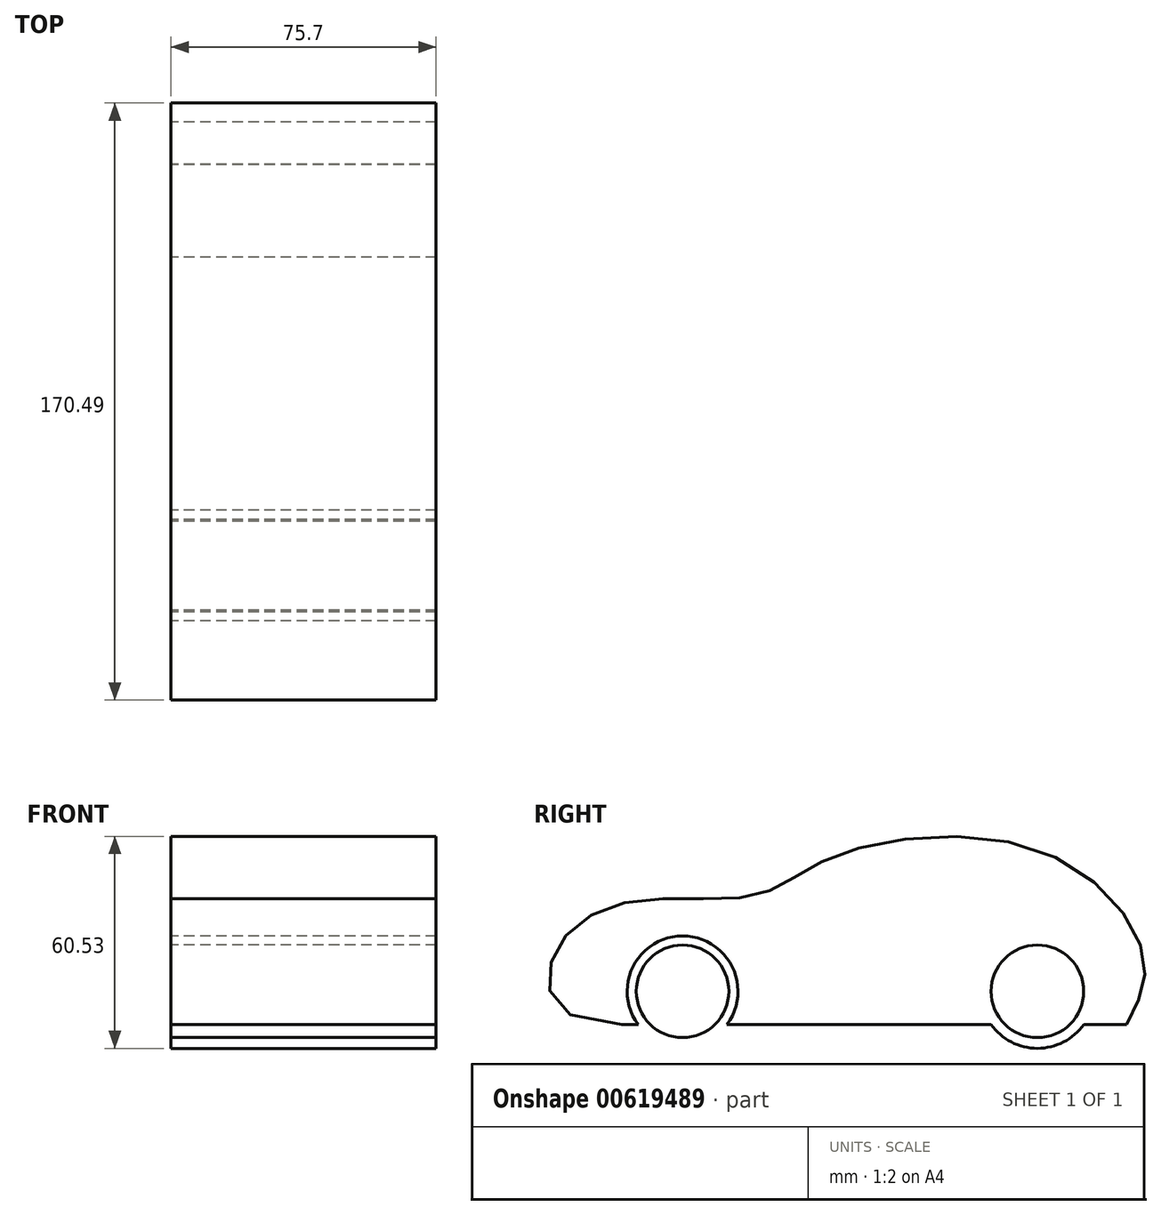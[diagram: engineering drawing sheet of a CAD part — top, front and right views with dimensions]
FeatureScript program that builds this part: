
annotation { "Feature Type Name" : "Feature", "Feature Type Description" : "" }
export const myFeature = defineFeature(function(context is Context, id is Id, definition is map)
    precondition{}
    {
        {
            var Q0;
            Q0=qCreatedBy(makeId("Right.planeOp"),FACE);
            var sketch = newSketch(context, id + "F0", { "sketchPlane" : qUnion([Q0])});
            skCircle(sketch, "E0", {"center": v(-50.67, 13.53) * mm, "radius": 13.22 * mm});
            skLineSegment(sketch, "E1", {"start": v(0, 0) * mm, "end": v(0, 51.38) * mm, "construction": true});
            skCircle(sketch, "E2.MirrorC", {"center": v(50.67, 13.53) * mm, "radius": 13.22 * mm});
            skCircle(sketch, "E3", {"center": v(-50.67, 13.53) * mm, "radius": 15.81 * mm});
            skCircle(sketch, "E4", {"center": v(50.67, 13.53) * mm, "radius": 16.29 * mm});
            skLineSegment(sketch, "E5", {"start": v(-37.99, 4.09) * mm, "end": v(37.4, 4.09) * mm});
            skLineSegment(sketch, "E6", {"start": v(-63.34, 4.09) * mm, "end": v(-68.02, 4.09) * mm});
            skLineSegment(sketch, "E7", {"start": v(63.94, 4.09) * mm, "end": v(76.1, 4.09) * mm});
            skFitSpline(sketch, "E8", {"points": [v(-68.02, 4.09) * mm, v(-88.3, 21.66) * mm, v(-68.02, 38.68) * mm, v(-30.06, 40.84) * mm, v(-8.02, 51.86) * mm, v(53.45, 52.9) * mm, v(81.19, 22.53) * mm, v(76.1, 4.09) * mm], "startDerivative": vector(-462.47, 0) * mm, "endDerivative": vector(-91.11, -167.92) * mm});
            skSolve(sketch);
        }
        {
            var Q0;
            {var subQ1=sQuery(id+"F0.wireOp",EDGE,"E5");Q0=makeQuery(id+"F0.imprint","IMPRINT",FACE,{"disambiguationData":[TD([[makeQuery(id+"F0.imprint","IMPRINT",EDGE,{"derivedFrom":subQ1}),1.0]])]});}
            var Q1;
            Q1=makeQuery(id+"F0.imprint","IMPRINT",FACE,{"disambiguationData":[TD([[makeQuery(id+"F0.imprint","IMPRINT",EDGE,{"derivedFrom":sQuery(id+"F0.wireOp",EDGE,"E0")}),1.0]])]});
            var Q2;
            Q2=makeQuery(id+"F0.imprint","IMPRINT",FACE,{"disambiguationData":[TD([[makeQuery(id+"F0.imprint","IMPRINT",EDGE,{"derivedFrom":sQuery(id+"F0.wireOp",EDGE,"E2.MirrorC")}),-1.0]])]});
            extrude(context, id + "F1", {"entities" : qUnion([Q0, Q1, Q2]), "endBound" : BoundingType.SYMMETRIC, "depth" : 75.7 * mm, "offsetDistance" : 25.4 * mm});
        }
    });
